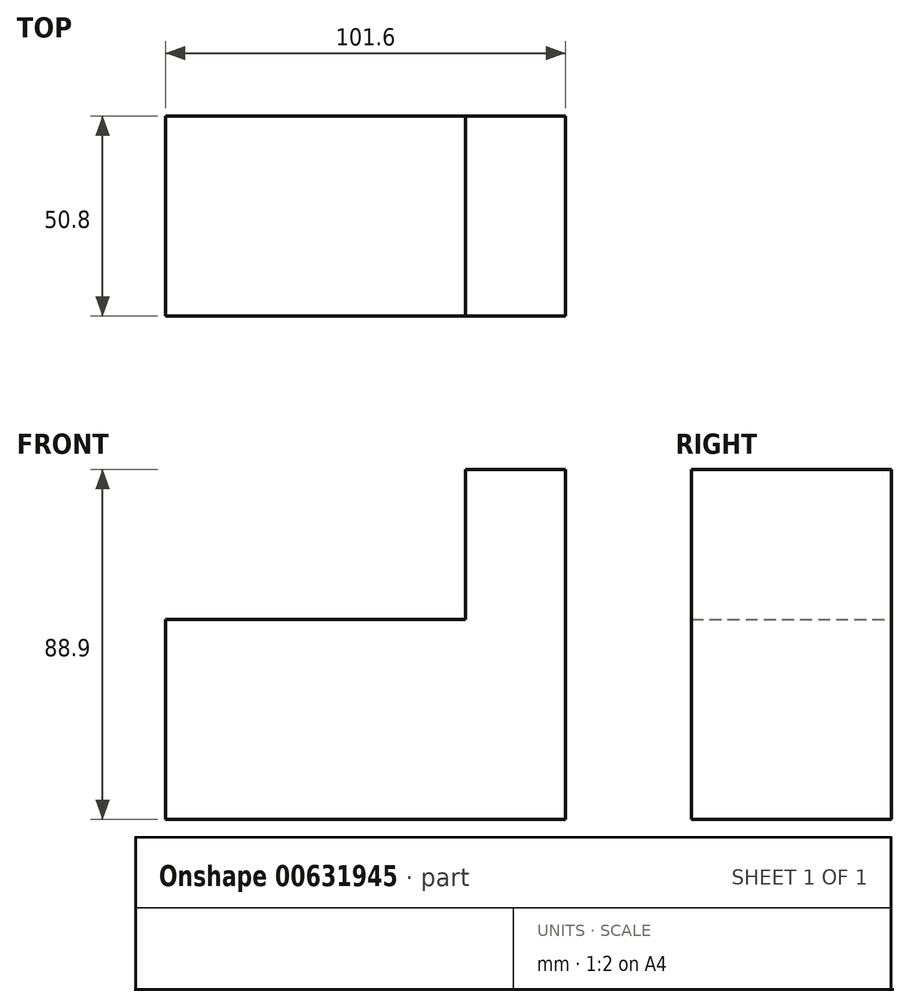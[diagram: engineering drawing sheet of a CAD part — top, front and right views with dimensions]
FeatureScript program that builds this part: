
annotation { "Feature Type Name" : "Feature", "Feature Type Description" : "" }
export const myFeature = defineFeature(function(context is Context, id is Id, definition is map)
    precondition{}
    {
        {
            var Q0;
            Q0=qCreatedBy(makeId("Front.planeOp"),FACE);
            var sketch = newSketch(context, id + "F0", { "sketchPlane" : qUnion([Q0])});
            skLineSegment(sketch, "E0.bottom", {"start": v(-38.1, 25.4) * mm, "end": v(38.1, 25.4) * mm});
            skLineSegment(sketch, "E0.top", {"start": v(-38.1, -25.4) * mm, "end": v(38.1, -25.4) * mm});
            skLineSegment(sketch, "E0.left", {"start": v(-38.1, 25.4) * mm, "end": v(-38.1, -25.4) * mm});
            skLineSegment(sketch, "E0.right", {"start": v(38.1, 25.4) * mm, "end": v(38.1, -25.4) * mm});
            skPoint(sketch, "E0.middle", {"position": v(0, 0) * mm});
            skLineSegment(sketch, "E1.bottom", {"start": v(38.1, -25.4) * mm, "end": v(63.5, -25.4) * mm});
            skLineSegment(sketch, "E1.top", {"start": v(38.1, 63.5) * mm, "end": v(63.5, 63.5) * mm});
            skLineSegment(sketch, "E1.left", {"start": v(38.1, -25.4) * mm, "end": v(38.1, 63.5) * mm});
            skLineSegment(sketch, "E1.right", {"start": v(63.5, -25.4) * mm, "end": v(63.5, 63.5) * mm});
            skSolve(sketch);
        }
        {
            var Q0;
            {var subQ0=sQuery(id+"F0.wireOp",EDGE,"E0.bottom");Q0=makeQuery(id+"F0.imprint","IMPRINT",FACE,{"disambiguationData":[TD([[makeQuery(id+"F0.imprint","IMPRINT",EDGE,{"derivedFrom":subQ0}),-1.0]])]});}
            var Q1;
            {var subQ3=sQuery(id+"F0.wireOp",EDGE,"E1.bottom");Q1=makeQuery(id+"F0.imprint","IMPRINT",FACE,{"disambiguationData":[TD([[makeQuery(id+"F0.imprint","IMPRINT",EDGE,{"derivedFrom":subQ3}),1.0]])]});}
            extrude(context, id + "F1", {"entities" : qUnion([Q0, Q1]), "endBound" : BoundingType.SYMMETRIC, "depth" : 50.8 * mm, "offsetDistance" : 25.4 * mm});
        }
    });
